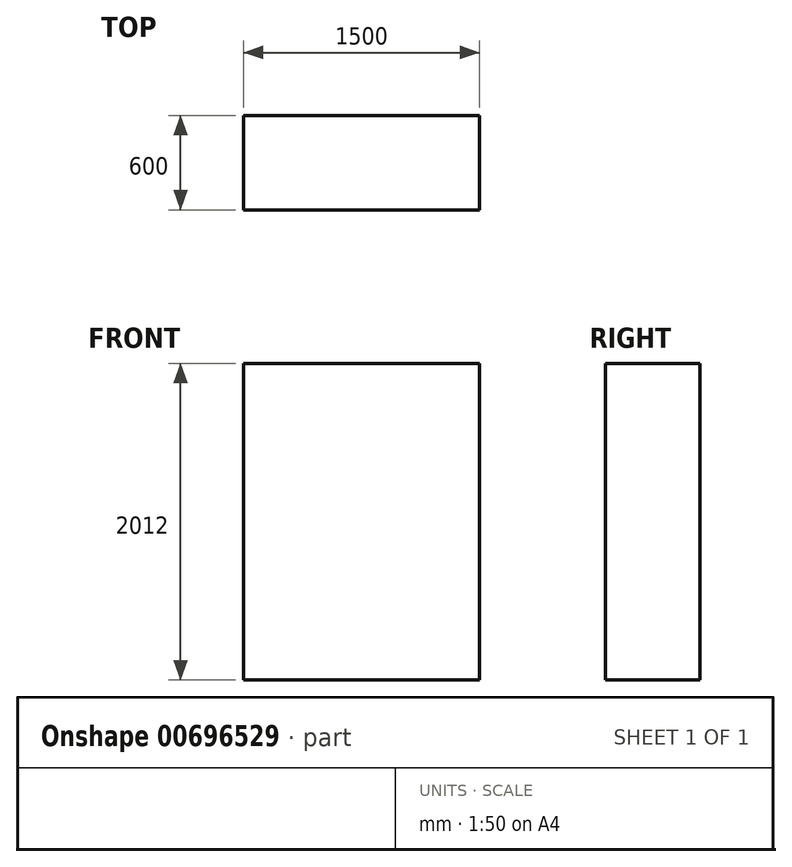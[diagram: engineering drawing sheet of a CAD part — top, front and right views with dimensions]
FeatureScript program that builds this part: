
annotation { "Feature Type Name" : "Feature", "Feature Type Description" : "" }
export const myFeature = defineFeature(function(context is Context, id is Id, definition is map)
    precondition{}
    {
        {
            var Q0;
            Q0=qCreatedBy(makeId("Top.planeOp"),FACE);
            var sketch = newSketch(context, id + "F0", { "sketchPlane" : qUnion([Q0])});
            skLineSegment(sketch, "E0.bottom", {"start": v(0, 0) * mm, "end": v(1500, 0) * mm});
            skLineSegment(sketch, "E0.top", {"start": v(0, 600) * mm, "end": v(1500, 600) * mm});
            skLineSegment(sketch, "E0.left", {"start": v(0, 0) * mm, "end": v(0, 600) * mm});
            skLineSegment(sketch, "E0.right", {"start": v(1500, 0) * mm, "end": v(1500, 600) * mm});
            skSolve(sketch);
        }
        {
            var Q0;
            Q0 = qSketchRegion(id + "F0", true);
            extrude(context, id + "F1", {"entities" : qUnion([Q0]), "depth" : 2012 * mm, "offsetDistance" : 25 * mm});
        }
    });
